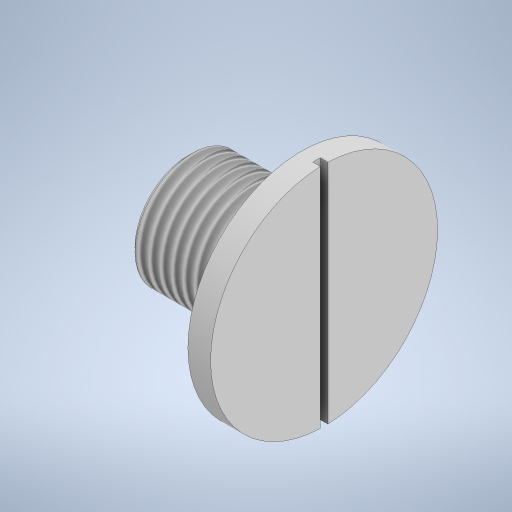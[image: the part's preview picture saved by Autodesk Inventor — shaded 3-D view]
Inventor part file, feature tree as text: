
AUTODESK INVENTOR PART (.ipt)
format: ipt  version: 2023 (Build 270158000, 158)  size: 264,704 bytes
history: native  units: mm
features: sketch x2, other x1, revolve x1, thread x1, chamfer x1, extrude x1
ambient origin geometry x8: Origin, YZ Plane, XZ Plane, XY Plane, X Axis, Y Axis, Z Axis, Center Point
bodies: Body1 (feature_tree)
feature tree (7):
  other  "Твердое тело1"
  revolve  "Вращение1"
  thread  "Резьба1"
  chamfer  "Фаска1"  Distance=15.0mm
  extrude  "Выдавливание1"  Depth=3.0mm
  sketch  "Эскиз1"
  sketch  "Эскиз2"
